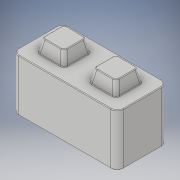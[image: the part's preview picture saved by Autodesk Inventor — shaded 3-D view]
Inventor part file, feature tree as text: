
AUTODESK INVENTOR PART (.ipt)
format: ipt  version: 2018 (Build 220112000, 112)  size: 423,936 bytes
history: native  units: in
note: dims shown in document units (in); Inventor stores cm internally (conversion verified against a paired STEP export)
features: chamfer x16, fillet x6, extrude x3, sketch x3
ambient origin geometry x8: Origin, YZ Plane, XZ Plane, XY Plane, X Axis, Y Axis, Z Axis, Center Point
bodies: Solid1 (feature_tree)
feature tree (28):
  extrude  "Extrusion1"  Depth=3.9in
  extrude  "Extrusion2"  Depth=1.0in
  extrude  "Extrusion3"  Depth=2.1in
  chamfer  "Chamfer1"  Distance=2.1in
  chamfer  "Chamfer2"  Distance=1.0in
  chamfer  "Chamfer3"  Distance=1.05in
  chamfer  "Chamfer4"  Distance=2.1in
  chamfer  "Chamfer5"  Distance=1.0in
  chamfer  "Chamfer6"  Distance=0.2in
  chamfer  "Chamfer7"  Distance=0.2in
  chamfer  "Chamfer8"  Distance=0.2in
  chamfer  "Chamfer9"  Distance=0.2in
  chamfer  "Chamfer10"  Distance=0.2in
  chamfer  "Chamfer11"  Distance=0.2in
  chamfer  "Chamfer12"  Distance=0.2in
  chamfer  "Chamfer13"  Distance=0.2in
  chamfer  "Chamfer14"  Distance=1.0in
  chamfer  "Chamfer15"  Distance=0.2in Angle=45.0deg
  chamfer  "Chamfer16"  Distance=0.2in Angle=45.0deg
  fillet  "Fillet1"  Radius=0.2in
  fillet  "Fillet2"  Radius=0.2in
  fillet  "Fillet3"  Radius=0.2in
  fillet  "Fillet4"  Radius=0.2in
  fillet  "Fillet5"  Radius=0.2in
  fillet  "Fillet6"  Radius=0.2in
  sketch  "Sketch1"  dims[d0=8.1in d1=3.9in]
  sketch  "Sketch2"  dims[d2=4.0in d3=0.0in d4=1.0in]
  sketch  "Sketch3"  dims[d5=1.05in d6=2.1in d7=2.1in d8=1.0in d9=1.05in d10=2.1in d11=1.0in d12=0.0in d13=0.2in d14=0.2in d15=0.2in d16=0.2in d17=0.2in d18=0.2in d19=0.2in d20=0.2in d21=1.0in d22=0.0in d23=0.2in d24=1.0in d25=45.0deg d26=0.2in d27=1.0in d28=45.0deg d29=0.2in d30=1.0in d31=45.0deg d32=0.2in d33=1.0in d34=45.0deg d35=0.2in d36=1.0in d37=45.0deg d38=0.2in d39=1.0in d40=45.0deg d41=0.2in d42=1.0in d43=45.0deg d44=0.2in d45=1.0in d46=45.0deg d47=0.2in d48=1.0in d49=45.0deg d50=0.2in d51=1.0in d52=45.0deg d53=0.2in d54=1.0in d55=45.0deg d56=0.2in d57=1.0in d58=45.0deg d59=0.2in d60=1.0in d61=45.0deg d62=0.2in d63=1.0in d64=45.0deg d65=0.2in d66=1.0in d67=45.0deg d68=0.2in d69=1.0in d70=45.0deg d71=0.5in d72=0.25in d73=0.25in d74=0.05in d75=0.05in d76=0.05in]
